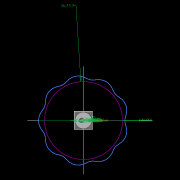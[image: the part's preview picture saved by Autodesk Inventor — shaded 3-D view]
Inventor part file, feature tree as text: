
AUTODESK INVENTOR PART (.ipt)
format: ipt  version: 2022.2 (Build 262287010, 287A)  size: 504,320 bytes
history: native  units: mm
features: other x19, extrude x16, sketch x10, pattern_circular x7, plane x3, fillet x2, move_body x2, revolve x2, draft x2, chamfer x2
ambient origin geometry x8: Origin, YZ Plane, XZ Plane, XY Plane, X Axis, Y Axis, Z Axis, Center Point
bodies: Solid5 (feature_tree)
feature tree (65):
  other  "CrossSection1"
  sketch  "Sketch7"  dims[d90=15.767323mm]
  other  "Roller1"
  other  "Roller2"
  sketch  "Sketch22"  dims[d167=8.972256mm]
  sketch  "Sketch2"  dims[d57=4.025mm]
  sketch  "Sketch23"  dims[d173=10.814812mm]
  other  "RevRoller1"
  fillet  "Fillet1"  Radius=13.336791mm
  pattern_circular  "Circular Pattern13"  Count=360  [1 undecoded]
  move_body  "Move Body7"
  revolve  "Revolution13"  [1 undecoded]
  fillet  "Fillet3"  Radius=0.025mm
  pattern_circular  "Circular Pattern14"  [2 undecoded]
  move_body  "Move Body6"
  revolve  "Revolution14"  [1 undecoded]
  plane  "Work Plane7"
  extrude  "Extrusion39"  Depth=10.461905mm
  other  "OuterRim_Top2"
  other  "OuterRim_Bottom2"
  extrude  "Rotor_Ring"  Depth=10.461905mm
  draft  "FaceDraft2"
  sketch  "Sketch30"  dims[d201=53.5mm d232=0.0mm d233=3600.0mm]
  plane  "Work Plane5"
  other  "Rotor Featurs"
  other  "RotorRim_Bottom"
  extrude  "Extrusion24"  Depth=10.461905mm
  extrude  "Extrusion25"  Depth=10.461905mm
  extrude  "Extrusion26"  Depth=10.461905mm
  pattern_circular  "Circular Pattern23"  Angle=90.0deg  [1 undecoded]
  sketch  "Sketch41"  dims[d346=0.025mm]
  extrude  "Extrusion27"  Depth=10.461905mm
  extrude  "Extrusion28"  Depth=10.461905mm
  pattern_circular  "Circular Pattern24"  Angle=360.0deg  [1 undecoded]
  extrude  "Extrusion29"  TaperAngle=30.0deg  [1 undecoded]
  extrude  "Extrusion30"  Depth=10.461905mm
  extrude  "Extrusion31"  Depth=10.461905mm
  pattern_circular  "Circular Pattern25"  [2 undecoded]
  sketch  "Sketch42"  dims[d347=0.1mm]
  extrude  "Extrusion32"  Depth=10.461905mm
  extrude  "Extrusion33"  TaperAngle=30.0deg  [1 undecoded]
  extrude  "Extrusion34"  TaperAngle=90.0deg  [1 undecoded]
  extrude  "Extrusion35"  Depth=10.461905mm
  pattern_circular  "Circular Pattern26"  Count=6  [1 undecoded]
  pattern_circular  "Circular Pattern27"  Angle=360.0deg  [1 undecoded]
  chamfer  "Chamfer1"  Angle=90.0deg  [1 undecoded]
  chamfer  "Chamfer2"  Distance=0.1mm
  draft  "FaceDraft4"
  plane  "Work Plane6"
  sketch  "Sketch43"  dims[d348=0.1mm]
  extrude  "Extrusion37"  Depth=10.461905mm
  extrude  "Extrusion38"  Depth=10.461905mm
  other  "2D Equation Curve1"
  sketch  "Sketch40"  dims[d343=17.374329mm d344=17.374602mm d345=0.025mm]
  other  "Work Axis6"
  other  "Work Axis7"
  other  "Work Axis8"
  other  "Work Axis9"
  other  "Work Axis10"
  other  "Work Point1"
  other  "Work Point2"
  other  "Work Point3"
  other  "Work Point4"
  other  "Work Point5"
  sketch  "Sketch44"  dims[d349=17.374602mm d350=17.374329mm d351=0.025mm d352=0.025mm d354=0.025mm d355=17.374329mm d356=17.374602mm d357=1.0mm d358=90.0deg d359=0.5mm d360=60.0mm d361=360.0deg d363=30.0deg d367=8.1mm d369=4.014775mm d370=0.025mm d371=1.0mm d372=30.0deg d373=90.0deg d374=0.5mm d375=60.0mm d376=360.0deg d378=90.0deg d379=0.1mm d380=0.025mm d381=0.025mm d382=0.025mm d383=0.025mm d384=10.461905mm d385=0.0mm d386=0.0mm d391=1.0mm d392=53.5mm d393=1.5mm d394=1.5mm d395=1.5mm d396=1.5mm d397=90.0deg d398=90.0deg d399=90.0deg d400=53.5mm d401=10.461905mm d402=0.0mm d486=0.436332mm d487=0.5mm d488=2.0mm d489=0.0mm d490=20.0mm d495=2.5mm d496=8.0mm d506=13.856406mm d507=55.5mm d508=8.0mm d509=0.05mm d510=2.5mm d511=30.0deg d512=12.0mm d513=6.0mm d514=0.2mm d515=30.0deg d516=131.0mm d517=65.5mm d518=0.2mm d519=100.0mm d520=120.0mm d521=2.0mm d522=150.0mm d530=50.0mm d531=5.5mm d532=5.5mm d533=5.5mm d534=85.75mm d535=73.5mm d536=61.25mm d537=24.5mm d538=3.0mm d539=2.4mm d540=0.0mm d541=0.0mm d542=0.0mm d543=5.5mm d544=3.0mm d545=0.0mm d546=90.0mm d547=360.0deg d549=3.0mm d550=3.0mm d551=2.4mm d552=0.0mm d553=5.230953mm d554=0.0mm d555=2.4mm d556=0.0mm d557=5.230953mm d558=0.0mm d559=5.230953mm d560=0.0mm d561=90.0mm d562=360.0deg d564=60.0mm d565=360.0deg d567=5.5mm d568=5.5mm d569=3.0mm d570=0.0mm d571=5.230953mm d572=0.0mm d573=3.0mm d574=0.0mm d575=5.230953mm d576=0.0mm d577=90.0mm d578=360.0deg d580=60.0mm d581=360.0deg d584=20.0mm d585=8.0mm d587=1.75mm d589=3.0mm d592=2.0mm d593=12.0mm d594=12.0mm d600=0.5mm d601=2.0mm d602=45.0deg d603=0.5mm d604=2.0mm d605=45.0deg d606=0.436332mm d607=0.5mm d608=0.0mm d609=20.0mm d611=360.0deg d613=0.0mm d614=0.0mm d615=20.0mm d616=2.5mm d617=7.0mm d618=0.0mm d619=0.0mm d16=0.872665mm d17=0.872665mm d49=0.872665mm d50=0.872665mm d51=0.872665mm d52=0.872665mm d236=0.5mm d237=0.872665mm d238=0.5mm d239=0.872665mm d282=1.0mm d283=1.0mm d284=1.0mm d285=0.15mm d286=0.25mm d287=0.375mm d288=14.3117mm d289=0.75mm d290=20.594885mm d291=0.0625mm d292=0.75mm d293=0.375mm d405=0.5mm d406=0.872665mm d407=0.5mm d408=0.872665mm d413=0.5mm d414=0.872665mm d415=0.5mm d416=0.872665mm d417=0.5mm d418=0.872665mm d419=0.5mm d420=0.872665mm d421=0.872665mm d431=0.5mm d432=0.872665mm d433=0.5mm d434=0.872665mm d471=0.5mm d472=0.872665mm d473=0.5mm d474=0.872665mm d497=0.5mm d498=0.872665mm d499=0.5mm d500=0.872665mm d590=0.5mm d591=0.872665mm]
note: 15 required parameter values undecoded (feature->parameter linkage not recoverable at this tier; creation-order binding heuristic only, values carry confidence <= 0.55)